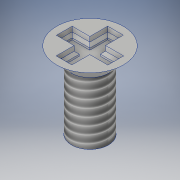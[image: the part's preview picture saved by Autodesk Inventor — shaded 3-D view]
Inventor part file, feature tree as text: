
AUTODESK INVENTOR PART (.ipt)
format: ipt  version: 2018 (Build 220112000, 112)  size: 206,848 bytes
history: native  units: in
note: dims shown in document units (in); Inventor stores cm internally (conversion verified against a paired STEP export)
features: sketch x3, extrude x2, revolve x1, thread x1, shell x1, chamfer x1
ambient origin geometry x8: Origin, YZ Plane, XZ Plane, XY Plane, X Axis, Y Axis, Z Axis, Center Point
bodies: Solid1 (feature_tree)
feature tree (9):
  revolve  "Revolution1"  [1 undecoded]
  thread  "Thread1"  [1 undecoded]
  extrude  "Extrusion1"  Depth=0.032in
  shell  "Shell1"  Thickness=0.032in
  extrude  "Extrusion2"  Depth=0.0375in
  chamfer  "Chamfer1"  Distance=0.0075in
  sketch  "Sketch1"  dims[d0=0.0377in d3=0.0683in d4=90.0deg]
  sketch  "Sketch4"  dims[d5=1.0in d6=0.0in d7=0.11in d8=0.032in]
  sketch  "Sketch5"  dims[d9=0.01in d10=0.0in d11=0.0375in d12=0.0075in d13=135.0deg d14=0.0071in d15=0.0075in d16=0.0075in d17=0.0075in d18=0.0075in d19=0.0075in d20=0.0075in d21=45.0deg d22=0.0075in d23=45.0deg d24=0.0075in d25=45.0deg d26=0.0075in d27=45.0deg d28=0.0075in d29=45.0deg d30=0.009in d31=0.0in d32=0.0053in d33=0.125in d34=45.0deg]
note: 2 required parameter values undecoded (feature->parameter linkage not recoverable at this tier; creation-order binding heuristic only, values carry confidence <= 0.55)